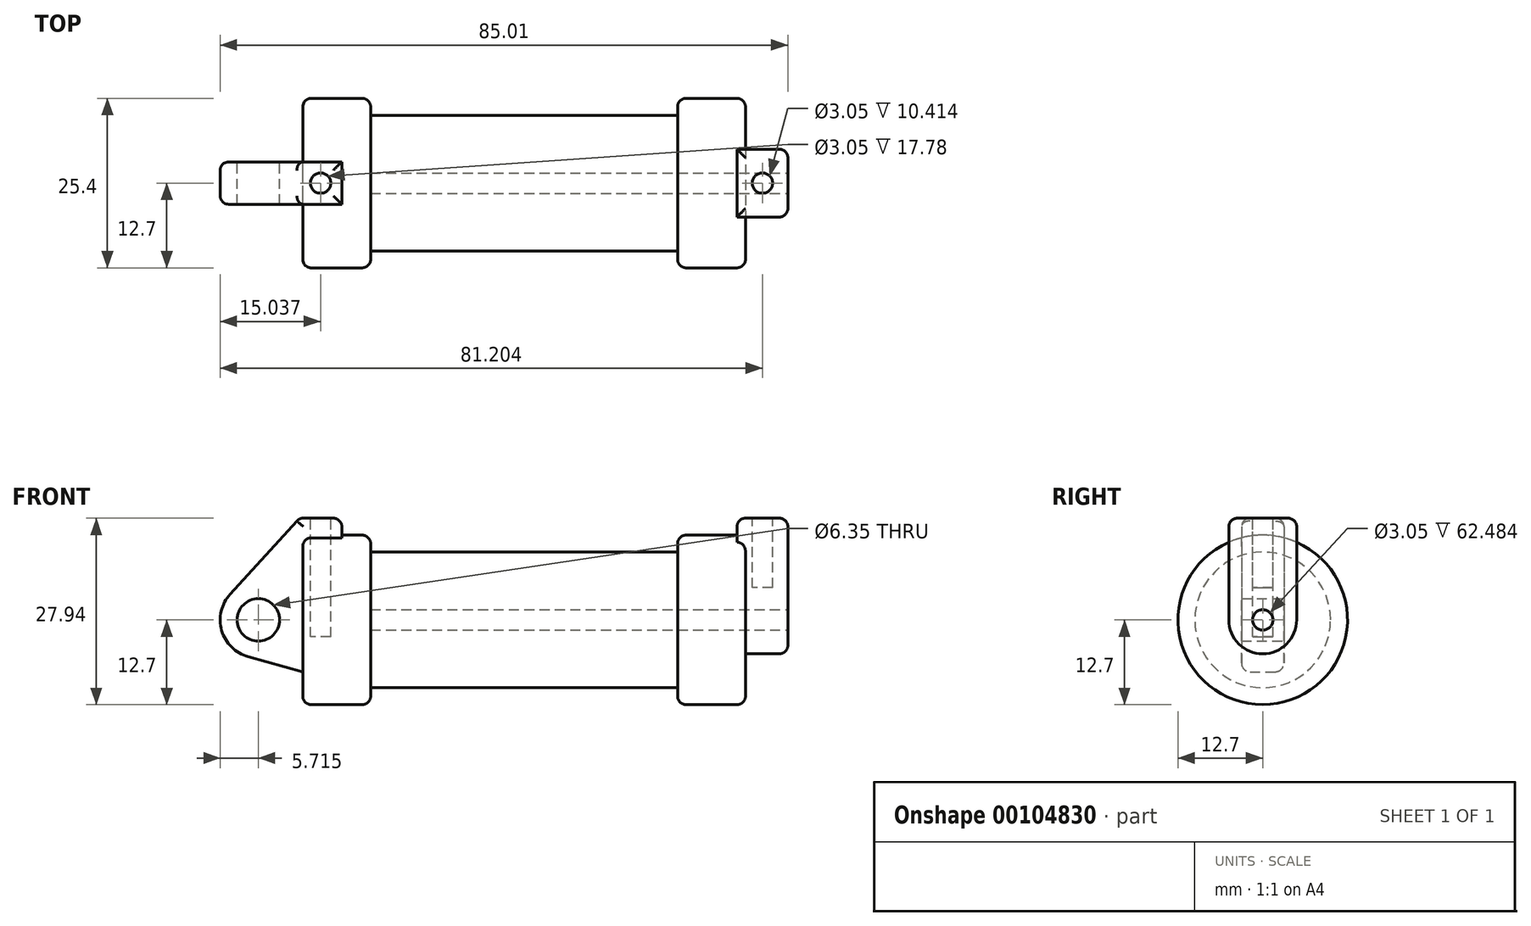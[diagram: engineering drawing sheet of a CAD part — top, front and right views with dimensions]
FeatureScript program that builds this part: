
annotation { "Feature Type Name" : "Feature", "Feature Type Description" : "" }
export const myFeature = defineFeature(function(context is Context, id is Id, definition is map)
    precondition{}
    {
        {
            var Q0;
            Q0=qCreatedBy(makeId("Front.planeOp"),FACE);
            var sketch = newSketch(context, id + "F0", { "sketchPlane" : qUnion([Q0])});
            skLineSegment(sketch, "E0", {"start": v(0, 0) * mm, "end": v(0, 12.7) * mm});
            skLineSegment(sketch, "E1", {"start": v(0, 12.7) * mm, "end": v(10.16, 12.7) * mm});
            skLineSegment(sketch, "E2", {"start": v(10.16, 12.7) * mm, "end": v(10.16, 10.16) * mm});
            skLineSegment(sketch, "E3", {"start": v(10.16, 10.16) * mm, "end": v(56.13, 10.16) * mm});
            skLineSegment(sketch, "E4", {"start": v(56.13, 10.16) * mm, "end": v(56.13, 12.7) * mm});
            skLineSegment(sketch, "E5", {"start": v(56.13, 12.7) * mm, "end": v(66.3, 12.7) * mm});
            skLineSegment(sketch, "E6", {"start": v(66.3, 12.7) * mm, "end": v(66.3, 0) * mm});
            skLineSegment(sketch, "E7", {"start": v(66.3, 0) * mm, "end": v(0, 0) * mm});
            skLineSegment(sketch, "E8", {"start": v(5.84, 15.24) * mm, "end": v(-0.5, 15.24) * mm});
            skLineSegment(sketch, "E9", {"start": v(-0.5, 15.24) * mm, "end": v(-10.88, 3.85) * mm});
            skLineSegment(sketch, "E10", {"start": v(0, 0) * mm, "end": v(-6.65, 0) * mm});
            skCircle(sketch, "E11", {"center": v(-6.65, 0) * mm, "radius": 5.72 * mm});
            skCircle(sketch, "E12", {"center": v(-6.65, 0) * mm, "radius": 3.18 * mm});
            skLineSegment(sketch, "E13", {"start": v(5.84, 15.24) * mm, "end": v(5.84, -9.4) * mm});
            skLineSegment(sketch, "E14", {"start": v(5.84, -9.4) * mm, "end": v(-8.18, -5.5) * mm});
            skSolve(sketch);
        }
        {
            var Q0;
            {var subQ0=sQuery(id+"F0.wireOp",EDGE,"E2");Q0=makeQuery(id+"F0.imprint","IMPRINT",FACE,{"disambiguationData":[TD([[makeQuery(id+"F0.imprint","IMPRINT",EDGE,{"derivedFrom":subQ0}),-1.0]])]});}
            var Q1;
            {var subQ0=sQuery(id+"F0.wireOp",EDGE,"E0");Q1=makeQuery(id+"F0.imprint","IMPRINT",FACE,{"disambiguationData":[TD([[makeQuery(id+"F0.imprint","IMPRINT",EDGE,{"derivedFrom":subQ0}),-1.0]])]});}
            var Q2;
            Q2=sQuery(id+"F0.wireOp",EDGE,"E7");
            revolve(context, id + "F1", {"entities" : qUnion([Q0, Q1]), "axis" : qUnion([Q2]), "revolveType" : RevolveType.FULL});
        }
        {
            var Q0;
            {var subQ0=sQuery(id+"F0.wireOp",EDGE,"E0");Q0=makeQuery(id+"F0.imprint","IMPRINT",FACE,{"disambiguationData":[TD([[makeQuery(id+"F0.imprint","IMPRINT",EDGE,{"derivedFrom":subQ0}),-1.0]])]});}
            var Q1;
            {var subQ3=sQuery(id+"F0.wireOp",EDGE,"E0");Q1=makeQuery(id+"F0.imprint","IMPRINT",FACE,{"disambiguationData":[TD([[makeQuery(id+"F0.imprint","IMPRINT",EDGE,{"derivedFrom":subQ3}),1.0]])]});}
            var Q2;
            {var subQ0=sQuery(id+"F0.wireOp",EDGE,"E14");Q2=makeQuery(id+"F0.imprint","IMPRINT",FACE,{"disambiguationData":[TD([[makeQuery(id+"F0.imprint","IMPRINT",EDGE,{"derivedFrom":subQ0}),-1.0]])]});}
            var Q3;
            {var subQ4=sQuery(id+"F0.wireOp",EDGE,"E12");Q3=makeQuery(id+"F0.imprint","IMPRINT",FACE,{"disambiguationData":[TD([[makeQuery(id+"F0.imprint","IMPRINT",EDGE,{"derivedFrom":subQ4}),-1.0]])]});}
            extrude(context, id + "F2", {"entities" : qUnion([Q0, Q1, Q2, Q3]), "operationType" : NewBodyOperationType.ADD, "endBound" : BoundingType.SYMMETRIC, "depth" : 6.35 * mm});
        }
        {
            var Q0;
            Q0=makeQuery(id+"F1.opRevolve","SWEPT_FACE",FACE,{"disambiguationData":[OSD([sQuery(id+"F0.wireOp",EDGE,"E6")])]});
            var sketch = newSketch(context, id + "F3", { "sketchPlane" : qUnion([Q0])});
            skCircle(sketch, "E15", {"center": v(0, 0) * mm, "radius": 1.52 * mm});
            skCircle(sketch, "E16", {"center": v(0, 0) * mm, "radius": 5.08 * mm});
            skLineSegment(sketch, "E17", {"start": v(-5.08, 0) * mm, "end": v(-5.08, 15.24) * mm});
            skLineSegment(sketch, "E18", {"start": v(5.08, 0) * mm, "end": v(5.08, 15.24) * mm});
            skLineSegment(sketch, "E19", {"start": v(5.08, 15.24) * mm, "end": v(-5.08, 15.24) * mm});
            skSolve(sketch);
        }
        {
            var Q0;
            Q0 = qSketchRegion(id + "F3", true);
            extrude(context, id + "F4", {"entities" : qUnion([Q0]), "operationType" : NewBodyOperationType.ADD, "oppositeDirection" : true, "depth" : 1.27 * mm, "hasSecondDirection" : true, "secondDirectionOppositeDirection" : false, "secondDirectionDepth" : 6.35 * mm});
        }
        {
            var Q0;
            Q0=makeQuery(id+"F4.opExtrude","SWEPT_FACE",FACE,{"disambiguationData":[OSD([sQuery(id+"F3.wireOp",EDGE,"E19")])]});
            var sketch = newSketch(context, id + "F5", { "sketchPlane" : qUnion([Q0])});
            skCircle(sketch, "E20", {"center": v(68.83, 0) * mm, "radius": 1.52 * mm});
            skPoint(sketch, "E20.centerSnap0", {"position": v(68.83, 5.08) * mm});
            skPoint(sketch, "E20.centerSnap1", {"position": v(72.64, 0) * mm});
            skSolve(sketch);
        }
        {
            var Q0;
            Q0 = qSketchRegion(id + "F5", true);
            extrude(context, id + "F6", {"entities" : qUnion([Q0]), "operationType" : NewBodyOperationType.REMOVE, "oppositeDirection" : true, "depth" : 10.4 * mm});
        }
        {
            var Q0;
            Q0=makeQuery(id+"F2.opExtrude","SWEPT_FACE",FACE,{"disambiguationData":[OSD([sQuery(id+"F0.wireOp",EDGE,"E8")])]});
            var sketch = newSketch(context, id + "F7", { "sketchPlane" : qUnion([Q0])});
            skCircle(sketch, "E21", {"center": v(2.67, 0) * mm, "radius": 1.52 * mm});
            skPoint(sketch, "E21.centerSnap0", {"position": v(5.84, 0) * mm});
            skPoint(sketch, "E21.centerSnap1", {"position": v(2.67, 3.18) * mm});
            skSolve(sketch);
        }
        {
            var Q0;
            Q0 = qSketchRegion(id + "F7", true);
            extrude(context, id + "F8", {"entities" : qUnion([Q0]), "operationType" : NewBodyOperationType.REMOVE, "oppositeDirection" : true, "depth" : 17.78 * mm});
        }
        {
            var Q0;
            Q0=sQuery(id+"F3.wireOp",EDGE,"E15");
            extrude(context, id + "F9", {"bodyType" : ToolBodyType.SURFACE, "surfaceEntities" : qUnion([Q0]), "oppositeDirection" : true, "depth" : 0.47 * mm});
        }
        {
            var Q0;
            Q0=makeQuery(id+"F4.boolean.opBoolean","SPLIT",FACE,{"disambiguationData":[TD([makeQuery(id+"F4.opExtrude","SWEPT_FACE",FACE,{"disambiguationData":[OSD([sQuery(id+"F3.wireOp",EDGE,"E15")])]})])],"derivedFrom":makeQuery(id+"F1.opRevolve","SWEPT_FACE",FACE,{"disambiguationData":[OSD([sQuery(id+"F0.wireOp",EDGE,"E6")])]})});
            var Q1;
            Q1=makeQuery(id+"F1.opRevolve","SWEPT_FACE",FACE,{"disambiguationData":[OSD([sQuery(id+"F0.wireOp",EDGE,"E2")])]});
            extrude(context, id + "F10", {"entities" : qUnion([Q0]), "operationType" : NewBodyOperationType.REMOVE, "endBound" : BoundingType.UP_TO_SURFACE, "oppositeDirection" : true, "endBoundEntityFace" : qUnion([Q1]), "depth" : 25.4 * mm});
        }
        {
            var Q0;
            Q0=makeQuery(id+"F2.opExtrude","CAP_EDGE",EDGE,{"disambiguationData":[OSD([sQuery(id+"F0.wireOp",EDGE,"E11")])],"isStart":true});
            var Q1;
            Q1=makeQuery(id+"F2.opExtrude","CAP_EDGE",EDGE,{"disambiguationData":[OSD([sQuery(id+"F0.wireOp",EDGE,"E9")])],"isStart":true});
            fillet(context, id + "F11", {"entities" : qUnion([Q0, Q1]), "radius" : 1.27 * mm, "tangentPropagation" : true, "allowEdgeOverflow" : false});
        }
        {
            var Q0;
            Q0=makeQuery(id+"F2.opExtrude","CAP_EDGE",EDGE,{"disambiguationData":[OSD([sQuery(id+"F0.wireOp",EDGE,"E9")])],"isStart":false});
            var Q1;
            Q1=makeQuery(id+"F2.opExtrude","CAP_EDGE",EDGE,{"disambiguationData":[OSD([sQuery(id+"F0.wireOp",EDGE,"E11")])],"isStart":false});
            fillet(context, id + "F12", {"entities" : qUnion([Q0, Q1]), "radius" : 1.27 * mm, "tangentPropagation" : true, "allowEdgeOverflow" : false});
        }
        {
            var Q0;
            Q0=makeQuery(id+"F2.opExtrude","CAP_EDGE",EDGE,{"disambiguationData":[OSD([sQuery(id+"F0.wireOp",EDGE,"E8")])],"isStart":true});
            var Q1;
            Q1=makeQuery(id+"F2.opExtrude","SWEPT_EDGE",EDGE,{"disambiguationData":[OSD([sQuery(id+"F0.wireOp",EDGE,"E8"),sQuery(id+"F0.wireOp",EDGE,"E13")])]});
            var Q2;
            Q2=makeQuery(id+"F2.opExtrude","CAP_EDGE",EDGE,{"disambiguationData":[OSD([sQuery(id+"F0.wireOp",EDGE,"E8")])],"isStart":false});
            fillet(context, id + "F13", {"entities" : qUnion([Q0, Q1, Q2]), "radius" : 1.27 * mm, "tangentPropagation" : true, "allowEdgeOverflow" : false});
        }
        {
            var Q0;
            Q0=makeQuery(id+"F4.opExtrude","CAP_EDGE",EDGE,{"disambiguationData":[OSD([sQuery(id+"F3.wireOp",EDGE,"E17")])],"isStart":true});
            var Q1;
            Q1=makeQuery(id+"F4.opExtrude","SWEPT_EDGE",EDGE,{"disambiguationData":[OSD([sQuery(id+"F3.wireOp",EDGE,"E17"),sQuery(id+"F3.wireOp",EDGE,"E19")])]});
            var Q2;
            Q2=makeQuery(id+"F4.opExtrude","CAP_EDGE",EDGE,{"disambiguationData":[OSD([sQuery(id+"F3.wireOp",EDGE,"E16")])],"isStart":true});
            var Q3;
            Q3=makeQuery(id+"F4.opExtrude","CAP_EDGE",EDGE,{"disambiguationData":[OSD([sQuery(id+"F3.wireOp",EDGE,"E18")])],"isStart":true});
            var Q4;
            Q4=makeQuery(id+"F4.opExtrude","SWEPT_EDGE",EDGE,{"disambiguationData":[OSD([sQuery(id+"F3.wireOp",EDGE,"E18"),sQuery(id+"F3.wireOp",EDGE,"E19")])]});
            var Q5;
            Q5=makeQuery(id+"F4.opExtrude","CAP_EDGE",EDGE,{"disambiguationData":[OSD([sQuery(id+"F3.wireOp",EDGE,"E19")])],"isStart":true});
            var Q6;
            Q6=makeQuery(id+"F4.opExtrude","CAP_EDGE",EDGE,{"disambiguationData":[OSD([sQuery(id+"F3.wireOp",EDGE,"E19")])],"isStart":false});
            fillet(context, id + "F14", {"entities" : qUnion([Q0, Q1, Q2, Q3, Q4, Q5, Q6]), "radius" : 1.27 * mm, "tangentPropagation" : true, "allowEdgeOverflow" : false});
        }
        {
            var Q0;
            Q0=makeQuery(id+"F1.opRevolve","SWEPT_EDGE",EDGE,{"disambiguationData":[OSD([sQuery(id+"F0.wireOp",EDGE,"E5"),sQuery(id+"F0.wireOp",EDGE,"E6")])]});
            var Q1;
            Q1=makeQuery(id+"F1.opRevolve","SWEPT_EDGE",EDGE,{"disambiguationData":[OSD([sQuery(id+"F0.wireOp",EDGE,"E4"),sQuery(id+"F0.wireOp",EDGE,"E5")])]});
            fillet(context, id + "F15", {"entities" : qUnion([Q0, Q1]), "radius" : 1.27 * mm, "tangentPropagation" : true, "allowEdgeOverflow" : false});
        }
        {
            var Q0;
            Q0=makeQuery(id+"F1.opRevolve","SWEPT_EDGE",EDGE,{"disambiguationData":[OSD([sQuery(id+"F0.wireOp",EDGE,"E1"),sQuery(id+"F0.wireOp",EDGE,"E2")])]});
            var Q1;
            Q1=makeQuery(id+"F1.opRevolve","SWEPT_EDGE",EDGE,{"disambiguationData":[OSD([sQuery(id+"F0.wireOp",EDGE,"E0"),sQuery(id+"F0.wireOp",EDGE,"E1")])]});
            fillet(context, id + "F16", {"entities" : qUnion([Q0, Q1]), "radius" : 1.27 * mm, "tangentPropagation" : true, "allowEdgeOverflow" : false});
        }
    });
